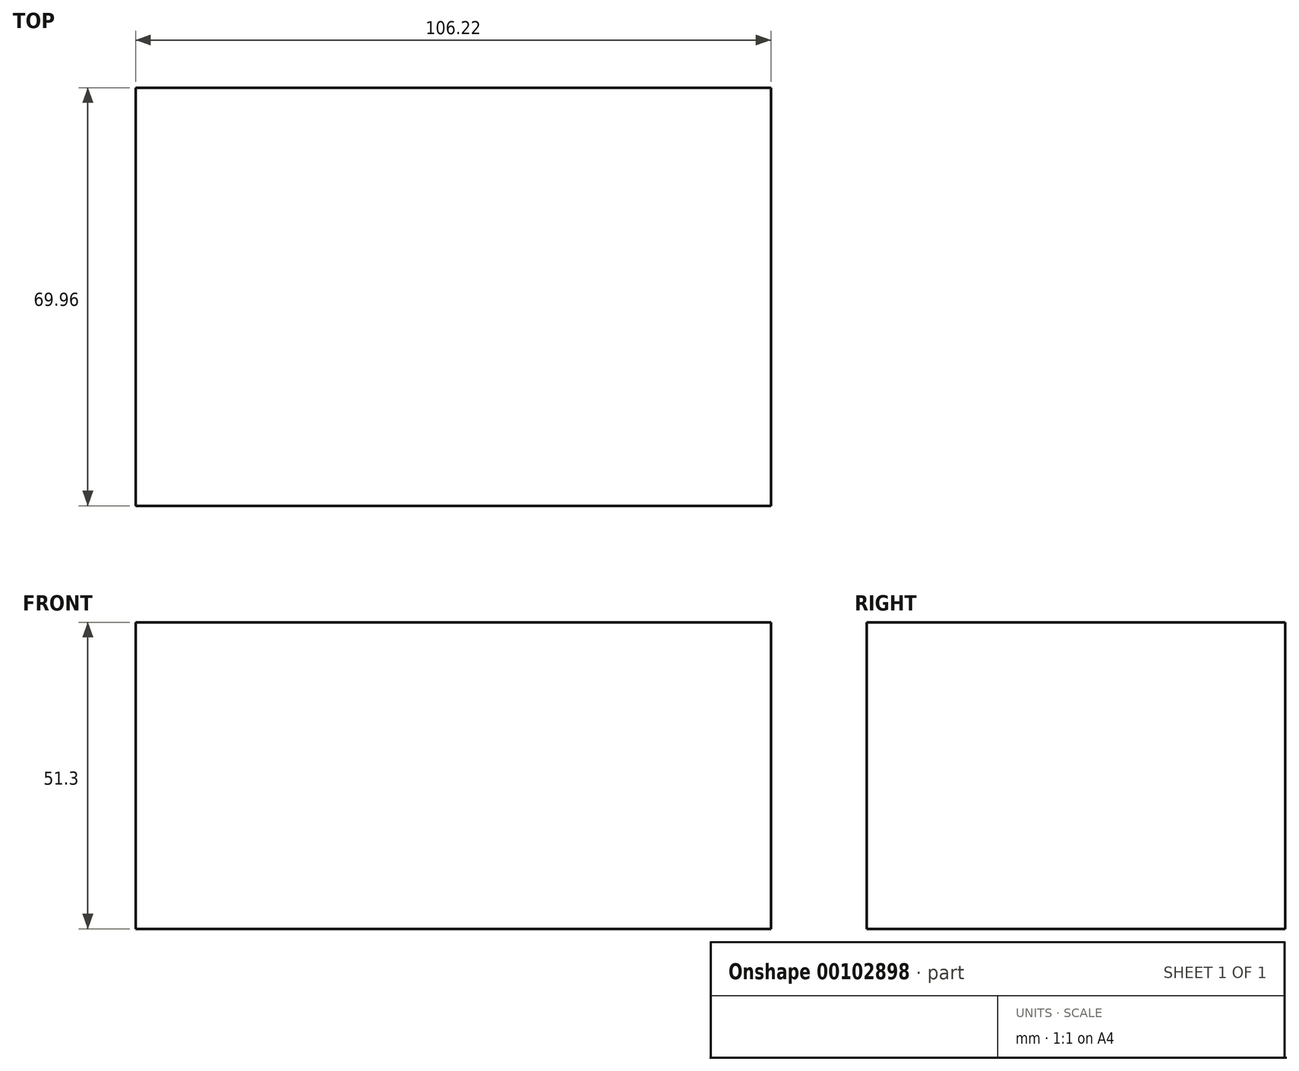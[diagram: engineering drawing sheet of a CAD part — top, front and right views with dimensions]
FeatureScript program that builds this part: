
annotation { "Feature Type Name" : "Feature", "Feature Type Description" : "" }
export const myFeature = defineFeature(function(context is Context, id is Id, definition is map)
    precondition{}
    {
        {
            var Q0;
            Q0=qCreatedBy(makeId("Front.planeOp"),FACE);
            var sketch = newSketch(context, id + "F0", { "sketchPlane" : qUnion([Q0])});
            skLineSegment(sketch, "E0.bottom", {"start": v(53.11, 25.65) * mm, "end": v(-53.11, 25.65) * mm});
            skLineSegment(sketch, "E0.top", {"start": v(53.11, -25.65) * mm, "end": v(-53.11, -25.65) * mm});
            skLineSegment(sketch, "E0.left", {"start": v(53.11, 25.65) * mm, "end": v(53.11, -25.65) * mm});
            skLineSegment(sketch, "E0.right", {"start": v(-53.11, 25.65) * mm, "end": v(-53.11, -25.65) * mm});
            skPoint(sketch, "E0.middle", {"position": v(0, 0) * mm});
            skSolve(sketch);
        }
        {
            var Q0;
            Q0 = qSketchRegion(id + "F0", true);
            extrude(context, id + "F1", {"entities" : qUnion([Q0]), "endBound" : BoundingType.SYMMETRIC, "depth" : 69.97 * mm});
        }
    });
